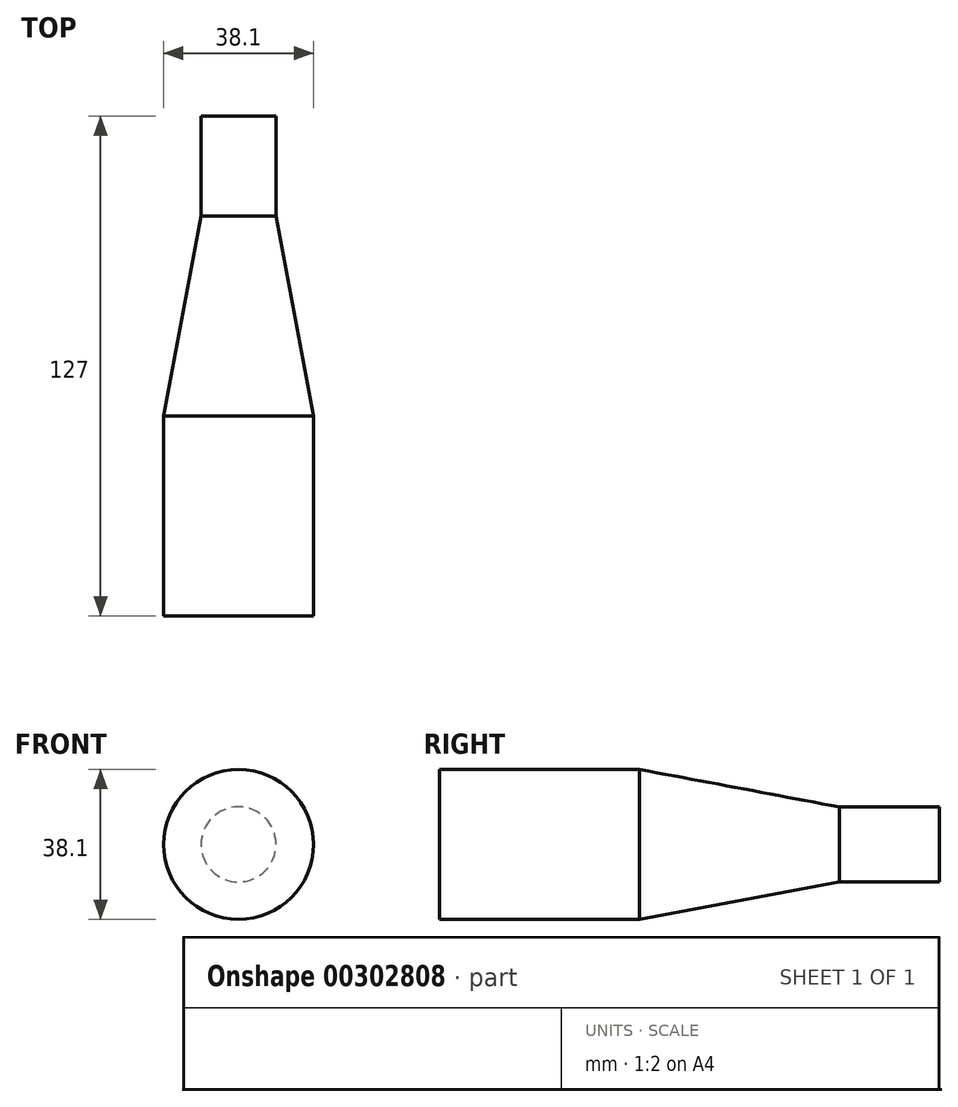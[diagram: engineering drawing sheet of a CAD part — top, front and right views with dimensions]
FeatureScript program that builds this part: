
annotation { "Feature Type Name" : "Feature", "Feature Type Description" : "" }
export const myFeature = defineFeature(function(context is Context, id is Id, definition is map)
    precondition{}
    {
        {
            var Q0;
            Q0=qCreatedBy(makeId("Right.planeOp"),FACE);
            var sketch = newSketch(context, id + "F0", { "sketchPlane" : qUnion([Q0])});
            skLineSegment(sketch, "E0", {"start": v(0, 0) * mm, "end": v(-127, 0) * mm});
            skLineSegment(sketch, "E1", {"start": v(-127, 0) * mm, "end": v(-127, 19.05) * mm});
            skLineSegment(sketch, "E2", {"start": v(-127, 19.05) * mm, "end": v(-76.2, 19.05) * mm});
            skLineSegment(sketch, "E3", {"start": v(-76.2, 19.05) * mm, "end": v(-25.4, 9.53) * mm});
            skLineSegment(sketch, "E4", {"start": v(-25.4, 9.53) * mm, "end": v(0, 9.53) * mm});
            skLineSegment(sketch, "E5", {"start": v(0, 9.53) * mm, "end": v(0, 0) * mm});
            skSolve(sketch);
        }
        {
            var Q0;
            Q0=makeQuery(id+"F0.imprint","IMPRINT",FACE,{"disambiguationData":[TD([[makeQuery(id+"F0.imprint","IMPRINT",EDGE,{"derivedFrom":sQuery(id+"F0.wireOp",EDGE,"E0")}),-1.0]])]});
            var Q1;
            Q1=sQuery(id+"F0.wireOp",EDGE,"E0");
            revolve(context, id + "F1", {"entities" : qUnion([Q0]), "axis" : qUnion([Q1]), "revolveType" : RevolveType.FULL});
        }
    });
